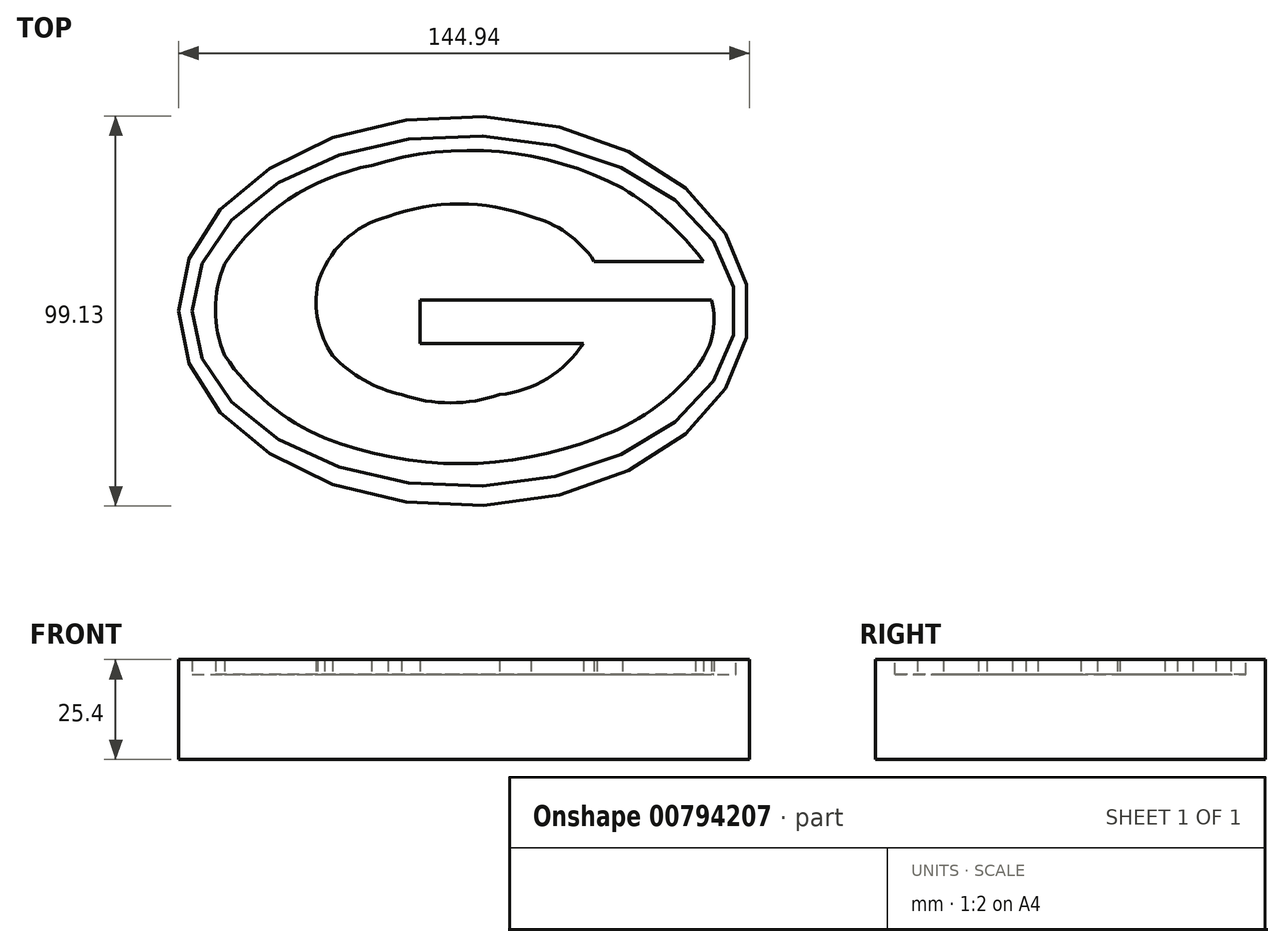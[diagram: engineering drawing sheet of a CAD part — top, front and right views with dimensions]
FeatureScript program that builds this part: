
annotation { "Feature Type Name" : "Feature", "Feature Type Description" : "" }
export const myFeature = defineFeature(function(context is Context, id is Id, definition is map)
    precondition{}
    {
        {
            var Q0;
            Q0=qCreatedBy(makeId("Top.planeOp"),FACE);
            var sketch = newSketch(context, id + "F0", { "sketchPlane" : qUnion([Q0])});
            skEllipse(sketch, "E0", {"center": v(0, 11.3) * mm, "majorRadius": 72.47 * mm, "minorRadius": 49.57 * mm, "majorAxis": v(-1, 0)});
            skLineSegment(sketch, "E1", {"start": v(30.32, 3.08) * mm, "end": v(-11.14, 3.08) * mm});
            skLineSegment(sketch, "E2", {"start": v(-11.14, 3.08) * mm, "end": v(-11.14, 14.05) * mm});
            skLineSegment(sketch, "E3", {"start": v(-11.14, 14.05) * mm, "end": v(62.88, 14.05) * mm});
            skArc(sketch, "E4", {"start": v(58.77, -3.43) * mm, "mid": v(63, 4.8) * mm, "end": v(62.88, 14.05) * mm});
            skArc(sketch, "E5", {"start": v(9.08, -9.94) * mm, "mid": v(21.17, -5.83) * mm, "end": v(30.32, 3.08) * mm});
            skArc(sketch, "E6", {"start": v(-15.93, -9.94) * mm, "mid": v(-3.43, -12.03) * mm, "end": v(9.08, -9.94) * mm});
            skArc(sketch, "E7", {"start": v(-33.4, 0) * mm, "mid": v(-25.4, -6.26) * mm, "end": v(-15.93, -9.94) * mm});
            skArc(sketch, "E8", {"start": v(-37.18, 18.16) * mm, "mid": v(-37.06, 8.71) * mm, "end": v(-33.4, 0) * mm});
            skArc(sketch, "E9", {"start": v(-19.36, 35.3) * mm, "mid": v(-30.56, 29.1) * mm, "end": v(-37.18, 18.16) * mm});
            skArc(sketch, "E10", {"start": v(16.96, 35.3) * mm, "mid": v(-1.2, 38.51) * mm, "end": v(-19.36, 35.3) * mm});
            skArc(sketch, "E11", {"start": v(33.07, 23.92) * mm, "mid": v(26.08, 31.12) * mm, "end": v(16.96, 35.3) * mm});
            skLineSegment(sketch, "E12", {"start": v(33.07, 23.92) * mm, "end": v(60.82, 23.92) * mm});
            skArc(sketch, "E13", {"start": v(33.75, -20.9) * mm, "mid": v(47.52, -13.97) * mm, "end": v(58.77, -3.43) * mm});
            skArc(sketch, "E14", {"start": v(-35.46, -20.9) * mm, "mid": v(-0.86, -27.47) * mm, "end": v(33.75, -20.9) * mm});
            skArc(sketch, "E15", {"start": v(-60.82, 0) * mm, "mid": v(-49.65, -12.28) * mm, "end": v(-35.46, -20.9) * mm});
            skArc(sketch, "E16", {"start": v(-60.82, 23.3) * mm, "mid": v(-63.14, 11.65) * mm, "end": v(-60.82, 0) * mm});
            skArc(sketch, "E17", {"start": v(-23.47, 48.31) * mm, "mid": v(-44.67, 39.58) * mm, "end": v(-60.82, 23.3) * mm});
            skArc(sketch, "E18", {"start": v(40.26, 42.49) * mm, "mid": v(8.98, 51.77) * mm, "end": v(-23.47, 48.31) * mm});
            skArc(sketch, "E19", {"start": v(60.82, 23.92) * mm, "mid": v(51.44, 34.2) * mm, "end": v(40.26, 42.49) * mm});
            skEllipse(sketch, "E20", {"center": v(0, 11.3) * mm, "majorRadius": 69.05 * mm, "minorRadius": 44.59 * mm, "majorAxis": v(-1, 0)});
            skSolve(sketch);
        }
        {
            var Q0;
            Q0=makeQuery(id+"F0.imprint","IMPRINT",FACE,{"disambiguationData":[TD([[makeQuery(id+"F0.imprint","IMPRINT",EDGE,{"derivedFrom":sQuery(id+"F0.wireOp",EDGE,"E0")}),1.0]])]});
            extrude(context, id + "F1", {"entities" : qUnion([Q0]), "depth" : 25.4 * mm, "offsetDistance" : 25.4 * mm});
        }
        {
            var Q0;
            Q0=makeQuery(id+"F0.imprint","IMPRINT",FACE,{"disambiguationData":[TD([[makeQuery(id+"F0.imprint","IMPRINT",EDGE,{"derivedFrom":sQuery(id+"F0.wireOp",EDGE,"E1")}),1.0]])]});
            extrude(context, id + "F2", {"entities" : qUnion([Q0]), "operationType" : NewBodyOperationType.ADD, "depth" : 21.59 * mm, "offsetDistance" : 25.4 * mm});
        }
        {
            var Q0;
            Q0=makeQuery(id+"F0.imprint","IMPRINT",FACE,{"disambiguationData":[TD([[makeQuery(id+"F0.imprint","IMPRINT",EDGE,{"derivedFrom":sQuery(id+"F0.wireOp",EDGE,"E1")}),-1.0]])]});
            extrude(context, id + "F3", {"entities" : qUnion([Q0]), "operationType" : NewBodyOperationType.ADD, "depth" : 25.4 * mm, "offsetDistance" : 25.4 * mm});
        }
    });
